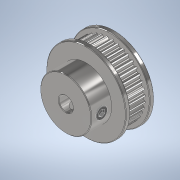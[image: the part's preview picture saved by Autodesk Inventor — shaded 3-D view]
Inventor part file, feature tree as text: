
AUTODESK INVENTOR PART (.ipt)
format: ipt  version: 2022 (Build 260153000, 153)  size: 631,808 bytes
history: native  units: in
note: dims shown in document units (in); Inventor stores cm internally (conversion verified against a paired STEP export)
features: sketch x5, other x3, extrude x2, plane x2, hole x2, chamfer x1, pattern_circular x1, projected_geometry x1
ambient origin geometry x8: Origin, YZ Plane, XZ Plane, XY Plane, X Axis, Y Axis, Z Axis, Center Point
bodies: Solid1 (feature_tree), Solid2 (feature_tree), Solid3 (feature_tree)
feature tree (17):
  other  "Pulley_1:1"
  extrude  "Extrusion1"  Depth=0.0079in TaperAngle=45.0deg
  plane  "Work Plane1"
  hole  "Hole2"  [1 undecoded]
  plane  "Work Plane2"
  hole  "Hole1"  [1 undecoded]
  chamfer  "Chamfer1"  [1 undecoded]
  extrude  "Extrusion2"  [1 undecoded]
  pattern_circular  "Circular Pattern1"  [2 undecoded]
  sketch  "Sketch1"  dims[d0=0.2815in d1=0.0in]
  sketch  "Sketch2"  dims[d2=0.1969in d3=0.75in d4=0.375in d5=0.25in d6=0.5635in d7=1.0in d8=0.8108in]
  sketch  "Sketch3"  dims[d9=0.1312in d10=0.75in d11=0.375in d12=0.25in d13=0.5635in d14=1.0in d15=0.8108in]
  sketch  "Sketch4"  dims[d16=0.1312in d17=0.75in d18=0.375in d19=0.25in d20=0.5635in d21=1.0in d22=0.8108in d23=0.0079in d24=0.0079in d25=45.0deg]
  sketch  "Sketch5"  dims[d26=1.0in d27=0.0in d28=15.748in d29=360.0deg]
  projected_geometry  "Projected Loop1"
  other  "Screw v1_1:1"
  other  "Screw v1 (1)_1:1"
note: 6 required parameter values undecoded (feature->parameter linkage not recoverable at this tier; creation-order binding heuristic only, values carry confidence <= 0.55)
